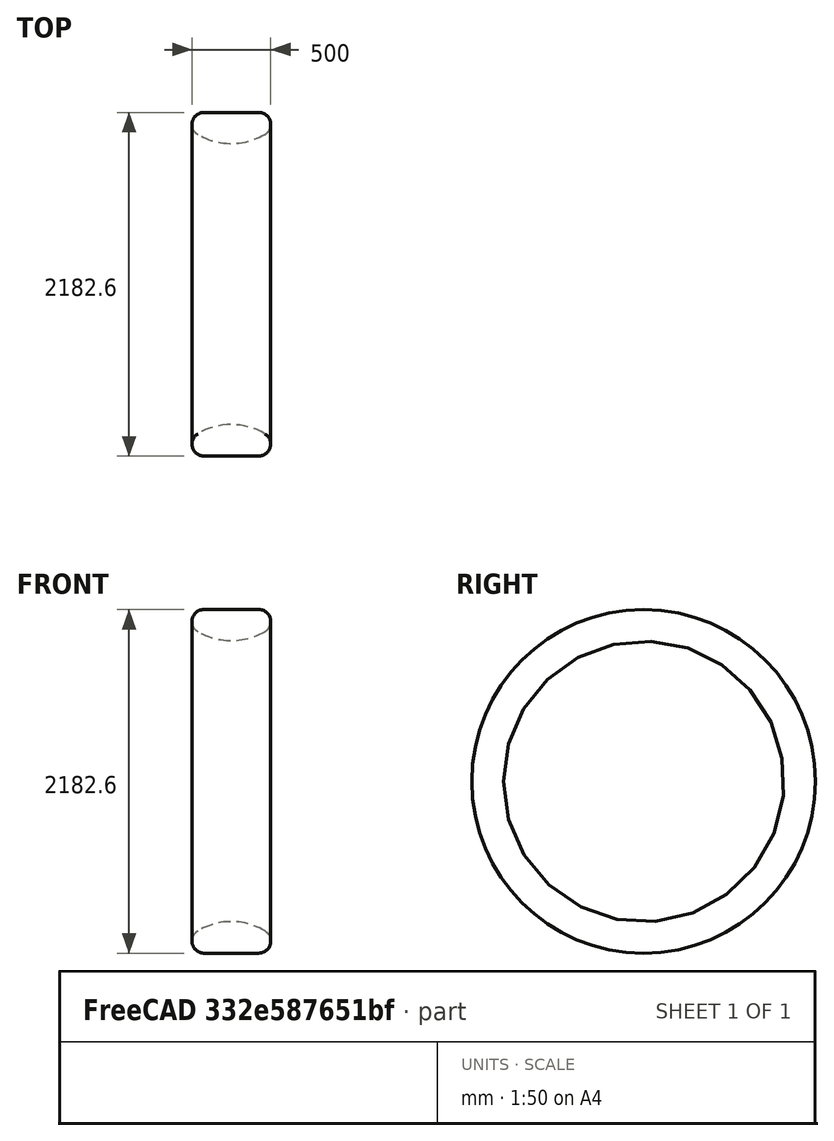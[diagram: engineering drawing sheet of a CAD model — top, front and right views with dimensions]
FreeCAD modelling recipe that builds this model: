
FCSTD DOCUMENT
Label: 4_Ring
objects: Sketcher::SketchObject×1, PartDesign::Revolution×1
note: 3 computed .brp shape members not serialized (recipe doc carries the construction recipe); baked Part::Feature solids carry a one-line shape summary decoded from their .brp

FEATURE [Sketcher::SketchObject] Sketch
  sketch-geometry (7):
    g0: LineSegment StartX=-230.499 StartY=-1091.3 StartZ=0 EndX=117.501 EndY=-1091.3 EndZ=0
    g1: ArcOfCircle CenterX=-230.499 CenterY=-1015.3 CenterZ=0 NormalX=0 NormalY=0 NormalZ=1 Radius=76 StartAngle=2.1091 EndAngle=4.71239
    g2: ArcOfCircle CenterX=117.501 CenterY=-1015.3 CenterZ=0 NormalX=0 NormalY=0 NormalZ=1 Radius=76 StartAngle=4.71239 EndAngle=7.31568
    g3: ArcOfCircle CenterX=-56.4986 CenterY=-1306.67 CenterZ=0 NormalX=0 NormalY=0 NormalZ=1 Radius=415.375 StartAngle=1.03249 EndAngle=2.1091
    g4: LineSegment StartX=-269.462 StartY=-950.048 StartZ=0 EndX=-269.454 EndY=-950.043 EndZ=0
    g5: LineSegment StartX=156.457 StartY=-950.043 StartZ=0 EndX=156.465 EndY=-950.048 EndZ=0
    g6: LineSegment [constr] StartX=-156.794 StartY=-891.3 StartZ=0 EndX=210.226 EndY=-891.3 EndZ=0
  constraints (16):
    c: Horizontal(g0)
    c: Tangent(g1,g0)
    c: Tangent(g0,g2)
    c: Radius(g1) = 76
    c: Radius(g2) = 76
    c: Tangent(g3,g4)
    c: Tangent(g1,g4)
    c: Tangent(g3,g5)
    c: Tangent(g5,g2)
    c: Distance(g4) = 0.01
    c: Distance(g5) = 0.01
    c: Horizontal(g6)
    c: Tangent(g6,g3)
    c: DistanceY(g6) = -891.3
    c: Distance(g1,g2) = 348
    c: Distance(g0,g6) = 200
FEATURE [PartDesign::Revolution] Revolution
  Angle = 360
  Axis = (1,0,0)
  Base = (0,0,0)
  ReferenceAxis = -> Sketch [H_Axis]
  Sketch = -> Sketch
